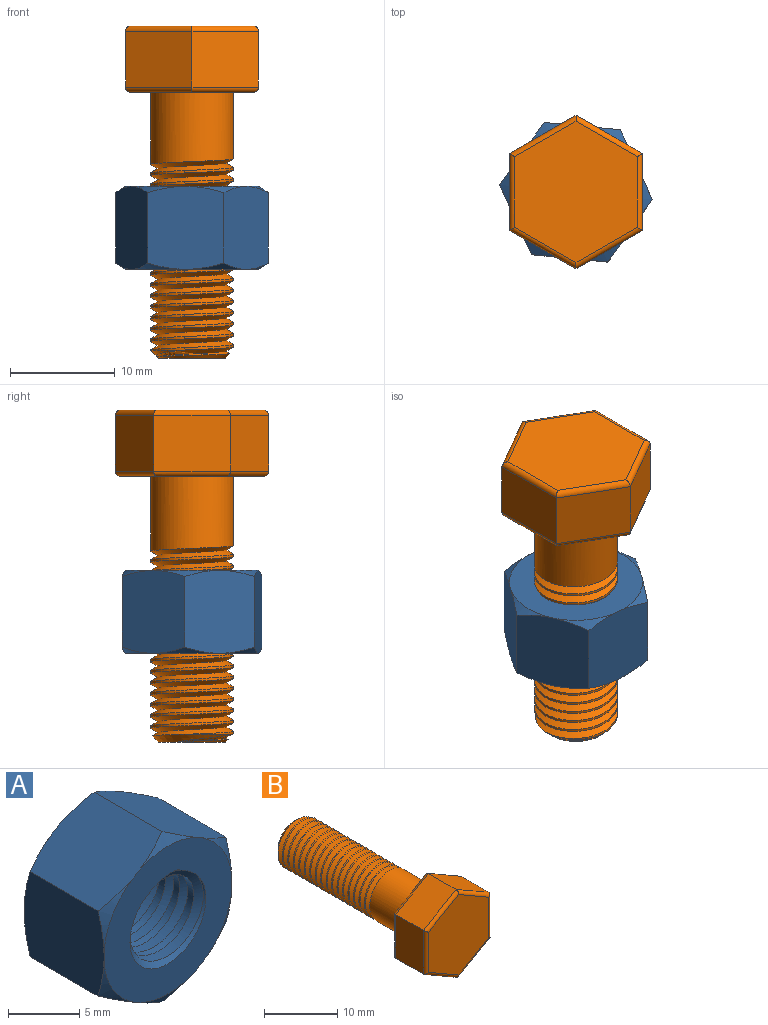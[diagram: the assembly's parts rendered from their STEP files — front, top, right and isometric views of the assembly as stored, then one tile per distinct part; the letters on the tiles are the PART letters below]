
ASSEMBLY  parts=2 mates=1
PART A: 25 faces, bbox 15.2x9.6x15.2 mm
  f0: plane 8.46x6.87mm, normal (-0.5,0,0.87), area 55.2mm2, adj f1,f5,f6,f7,f11,f16,f18,f22
  f1: plane 8.46x7.85mm, normal (-1,0,0), area 55.2mm2, adj f0,f2,f6,f7,f15,f16,f21,f22
  f2: plane 8.46x6.87mm, normal (-0.5,0,-0.87), area 55.2mm2, adj f1,f3,f6,f7,f14,f15,f20,f21
  f3: plane 8.46x6.87mm, normal (0.5,0,-0.87), area 55.2mm2, adj f2,f4,f6,f7,f13,f14,f19,f20
  f4: plane 8.46x7.85mm, normal (1,0,0), area 55.2mm2, adj f3,f5,f6,f7,f12,f13,f17,f19
  f5: plane 8.46x6.87mm, normal (0.5,0,0.87), area 55.2mm2, adj f0,f4,f6,f7,f11,f12,f17,f18
  f6: plane 12.76x12.74mm, normal (0,1,0), area 81.9mm2, adj f0,f1,f2,f3,f4,f5,f10,f17
  f7: plane 12.77x12.76mm, normal (0,-1,0), area 81.9mm2, adj f0,f1,f2,f3,f4,f5,f9,f11
  f8: cylinder r=3.26mm len=6.92mm, axis (0,1,0), area 60.9mm2, adj f9,f10,f23,f24
  f9: cone r=3.26mm half-angle=45deg, axis (0,-1,0), area 10.1mm2, adj f7,f8,f23,f24
  f10: cone r=3.77mm half-angle=45deg, axis (0,1,0), area 10.1mm2, adj f6,f8,f23,f24
  f11: cone r=6.36mm half-angle=58.5deg, axis (0,1,0), area 3.6mm2, adj f0,f5,f7
  f12: cone r=6.36mm half-angle=58.5deg, axis (0,1,0), area 3.6mm2, adj f4,f5,f7
  f13: cone r=6.36mm half-angle=58.5deg, axis (0,1,0), area 3.6mm2, adj f3,f4,f7
  f14: cone r=6.36mm half-angle=58.5deg, axis (0,1,0), area 3.6mm2, adj f2,f3,f7
  f15: cone r=6.36mm half-angle=58.5deg, axis (0,1,0), area 3.6mm2, adj f1,f2,f7
  f16: cone r=6.36mm half-angle=58.5deg, axis (0,1,0), area 3.6mm2, adj f0,f1,f7
  f17: cone r=6.36mm half-angle=58.5deg, axis (0,-1,0), area 3.6mm2, adj f4,f5,f6
  f18: cone r=6.36mm half-angle=58.5deg, axis (0,-1,0), area 3.6mm2, adj f0,f5,f6
  f19: cone r=6.36mm half-angle=58.5deg, axis (0,-1,0), area 3.6mm2, adj f3,f4,f6
  f20: cone r=6.36mm half-angle=58.5deg, axis (0,-1,0), area 3.6mm2, adj f2,f3,f6
  f21: cone r=6.36mm half-angle=58.5deg, axis (0,-1,0), area 3.6mm2, adj f1,f2,f6
  f22: cone r=6.36mm half-angle=58.5deg, axis (0,-1,0), area 3.6mm2, adj f0,f1,f6
  f23: bspline ~9.15x8.87mm, area 99.7mm2, adj f6,f7,f8,f9,f10,f24
  f24: bspline ~9.15x8.63mm, area 99.6mm2, adj f6,f7,f8,f9,f10,f23
PART B: 44 faces, bbox 12.9x32.4x14.9 mm
  f0: cylinder r=3.97mm len=7.94mm, axis (0,-1,0), area 172.2mm2, adj f1,f25,f40,f41,f42,f43
  f1: cylinder r=3.97mm len=7.94mm, axis (0,-1,0), area 5.7mm2, adj f0,f2,f40,f41
  f2: cylinder r=3.97mm len=7.94mm, axis (0,-1,0), area 5.7mm2, adj f1,f3,f40,f41
  f3: cylinder r=3.97mm len=7.94mm, axis (0,-1,0), area 5.7mm2, adj f2,f4,f40,f41
  f4: cylinder r=3.97mm len=7.94mm, axis (0,-1,0), area 5.7mm2, adj f3,f5,f40,f41
  f5: cylinder r=3.97mm len=7.94mm, axis (0,-1,0), area 5.7mm2, adj f4,f6,f40,f41
  f6: cylinder r=3.97mm len=7.94mm, axis (0,-1,0), area 5.7mm2, adj f5,f7,f40,f41
  f7: cylinder r=3.97mm len=7.94mm, axis (0,-1,0), area 5.7mm2, adj f6,f8,f40,f41
  f8: cylinder r=3.97mm len=7.94mm, axis (0,-1,0), area 5.7mm2, adj f7,f9,f40,f41
  f9: cylinder r=3.97mm len=7.94mm, axis (0,-1,0), area 5.7mm2, adj f8,f10,f40,f41
  f10: cylinder r=3.97mm len=7.94mm, axis (0,-1,0), area 5.7mm2, adj f9,f11,f40,f41
  f11: cylinder r=3.97mm len=7.94mm, axis (0,-1,0), area 5.7mm2, adj f10,f12,f40,f41
  f12: cylinder r=3.97mm len=7.94mm, axis (0,-1,0), area 5.7mm2, adj f11,f13,f40,f41
  f13: cylinder r=3.97mm len=7.94mm, axis (0,-1,0), area 5.7mm2, adj f12,f14,f40,f41
  f14: cylinder r=3.97mm len=7.94mm, axis (0,-1,0), area 5.7mm2, adj f13,f15,f40,f41
  f15: cylinder r=3.97mm len=7.94mm, axis (0,-1,0), area 5.7mm2, adj f14,f16,f40,f41
  f16: cylinder r=3.97mm len=7.94mm, axis (0,-1,0), area 5.7mm2, adj f15,f17,f40,f41
  f17: cylinder r=3.97mm len=3.83mm, axis (0,-1,0), area 0.6mm2, adj f16,f39,f41
  f18: plane 6.35x5.33mm, normal (-0.5,0,0.87), area 39.1mm2, adj f19,f23,f29,f35
  f19: plane 7.33x5.33mm, normal (-1,0,0), area 39.1mm2, adj f18,f20,f27,f33
  f20: plane 6.35x5.33mm, normal (-0.5,0,-0.87), area 39.1mm2, adj f19,f21,f28,f34
  f21: plane 6.35x5.33mm, normal (0.5,0,-0.87), area 39.1mm2, adj f20,f22,f30,f36
  f22: plane 7.33x5.33mm, normal (1,0,0), area 39.1mm2, adj f21,f23,f32,f38
  f23: plane 6.35x5.33mm, normal (0.5,0,0.87), area 39.1mm2, adj f18,f22,f31,f37
  f24: plane 13.49x11.68mm, normal (0,-1,0), area 118.2mm2, adj f33,f34,f35,f36,f37,f38
  f25: plane 13.49x11.68mm, normal (0,1,0), area 68.7mm2, adj f0,f27,f28,f29,f30,f31,f32
  f26: plane 6.41x6.41mm, normal (0,1,0), area 32.3mm2, adj f39
  f27: cylinder r=0.51mm len=7.33mm, axis (0,0,-1), area 5.6mm2, adj f19,f25,f28,f29
  f28: cylinder r=0.51mm len=6.6mm, axis (0.87,0,-0.5), area 5.6mm2, adj f20,f25,f27,f30
  f29: cylinder r=0.51mm len=6.6mm, axis (-0.87,0,-0.5), area 5.6mm2, adj f18,f25,f27,f31
  f30: cylinder r=0.51mm len=6.6mm, axis (0.87,0,0.5), area 5.6mm2, adj f21,f25,f28,f32
  f31: cylinder r=0.51mm len=6.6mm, axis (-0.87,0,0.5), area 5.6mm2, adj f23,f25,f29,f32
  f32: cylinder r=0.51mm len=7.33mm, axis (0,0,1), area 5.6mm2, adj f22,f25,f30,f31
  f33: cylinder r=0.51mm len=7.33mm, axis (0,0,1), area 5.6mm2, adj f19,f24,f34,f35
  f34: cylinder r=0.51mm len=6.6mm, axis (-0.87,0,0.5), area 5.6mm2, adj f20,f24,f33,f36
  f35: cylinder r=0.51mm len=6.6mm, axis (0.87,0,0.5), area 5.6mm2, adj f18,f24,f33,f37
  f36: cylinder r=0.51mm len=6.6mm, axis (-0.87,0,-0.5), area 5.6mm2, adj f21,f24,f34,f38
  f37: cylinder r=0.51mm len=6.6mm, axis (0.87,0,-0.5), area 5.6mm2, adj f23,f24,f35,f38
  f38: cylinder r=0.51mm len=7.33mm, axis (0,0,-1), area 5.6mm2, adj f22,f24,f36,f37
  f39: cone r=3.21mm half-angle=45deg, axis (0,-1,0), area 15mm2, adj f17,f26,f40,f41
  f40: bspline ~19.11x9.17mm, area 327.6mm2, adj f0,f1,f2,f3,f4,f5,f6,f7
  f41: bspline ~19.11x9.17mm, area 319.6mm2, adj f0,f1,f2,f3,f4,f5,f6,f7
  f42: plane 2.48x0.92mm, normal (0.5,0.87,0), area 1.3mm2, adj f0,f40,f43
  f43: plane 2.48x0.92mm, normal (0.5,-0.87,0), area 1.3mm2, adj f0,f41,f42
PLACE A rot(axis=(-0.96,-0.21,0.21),92.6deg) t=(0,0,-19.3)mm
PLACE B rot(axis=(-1,0,0),90deg) t=(0,0,-3.18)mm
MATE cylindrical B.f0 <-> A.f8  axis (0,0,-1) through (0,0,-31.75)mm
